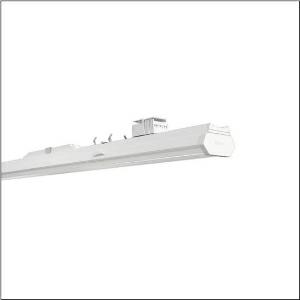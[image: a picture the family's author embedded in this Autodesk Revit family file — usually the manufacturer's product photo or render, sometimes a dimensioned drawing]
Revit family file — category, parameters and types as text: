
# Revit family: licross_r__11_protected_ho_51tp12dn4fxm3s_598f
name_source: partatom
category: Lighting Fixtures
units: mm (PartAtom-declared; Revit-internal decimal feet)

## family parameters
Cut with Voids When Loaded = No
Host = Face
Light Source = No
Part Type = Normal
Room Calculation Point = No
Round Connector Dimension = Use Diameter
Shared = No

## types (1)
- --- (1 x LED, 970 lm, 7.4 W, 4000K)
    Apparent Load = 7 VA
    CIE Flux Codes = 70 91 97 98 100
    Color Rendering = 80
    Color Temperature = 4000K
    Default Elevation = 1800 mm
    Description = Licross® 11 Protected HO, luminaire insert, of sheet steel, galvanised, coil coated, white, length: 1.500mm, width: 90mm, height: 101mm, LED rated luminous flux: 15.270lm, light colour: 840, control gear: DALI 2 (for two DALI lines), with plug, 6-pole, with phase selection, for trunking rail, 14-core, mains connection: 220..240V, AC, 50/60Hz, rated input power: 91W, for trunking rail, 14-core, internal wiring halogen-free, for emergency light function, converter,control gear: single battery element, battery: LiFePO4, 9Ah, primary light control with lens, of plastic, primary optical cover: cover, of PMMA, light emission: direct distribution, primary light characteristic: symmetric, protection rating (complete): IP64, insulation class (complete): insulation class I (protective earthing), certification: CE, UKCA, protection symbol: D if used in an environment with conductive dust loads with corresponding accessories, impact resistance: IK06, permissible ambient temperature for indoor applications: +5..+30°C, standard: EN 60598-2-22, LABS conformity tested according to VDMA 24364:2018-05, reducing of maximum allowable ambient temperature of 5°C with ceiling mounting, corresponds to IFS (International Featured Standards) requirements for safety and quality in the food industry, packaging unit: 1 piece
    Height = 92 mm
    Lamp = 1 x LED
    Lamp Light Flux = 970 lm
    Lamp Power = 7.4 W
    Lamp count = 1
    Length = 1500 mm
    Luminous efficacy = 131 lm/W
    Manufacturer = Siteco
    ModVariant = No
    Model = 51TP12DN4FXM3S
    Mounting Place = Ceiling
    Mounting Type = Pendant
    Number of Poles = 1
    OnlyDefault = Yes
    Power Factor = 1
    Product Name = Licross® 11 Protected HO
    Product group = luminaire insert | ceiling pendant
    ProductGroupID = 902
    Protection Class = Protection class I
    Protection Degree = IP 64
    RLX_Detail_Level = 1
    RLX_Emergency_Light_Flux = 0 lm
    RLX_Emergency_Type = 0
    RLX_Emergency_Type_DB = No
    RlxData = <blob elided: 24981 chars, md5=9e403475>
    Socket = socket
    Standby Power = 0 W
    System Light Flux = 970 lm
    System Power = 7 W
    Type Comments = : emergency light operation: 3 h
    Type Image = l_1256148.jpg
    URL = http://relux.com
    VarID = @adj_112541
    Voltage = 0 V
    Weight = 0.00 kg
    Width = 88 mm

## geometry (parser evidence)
native form markers: Blend x4, Sweep x10
no freeform markers — native parametric forms only
